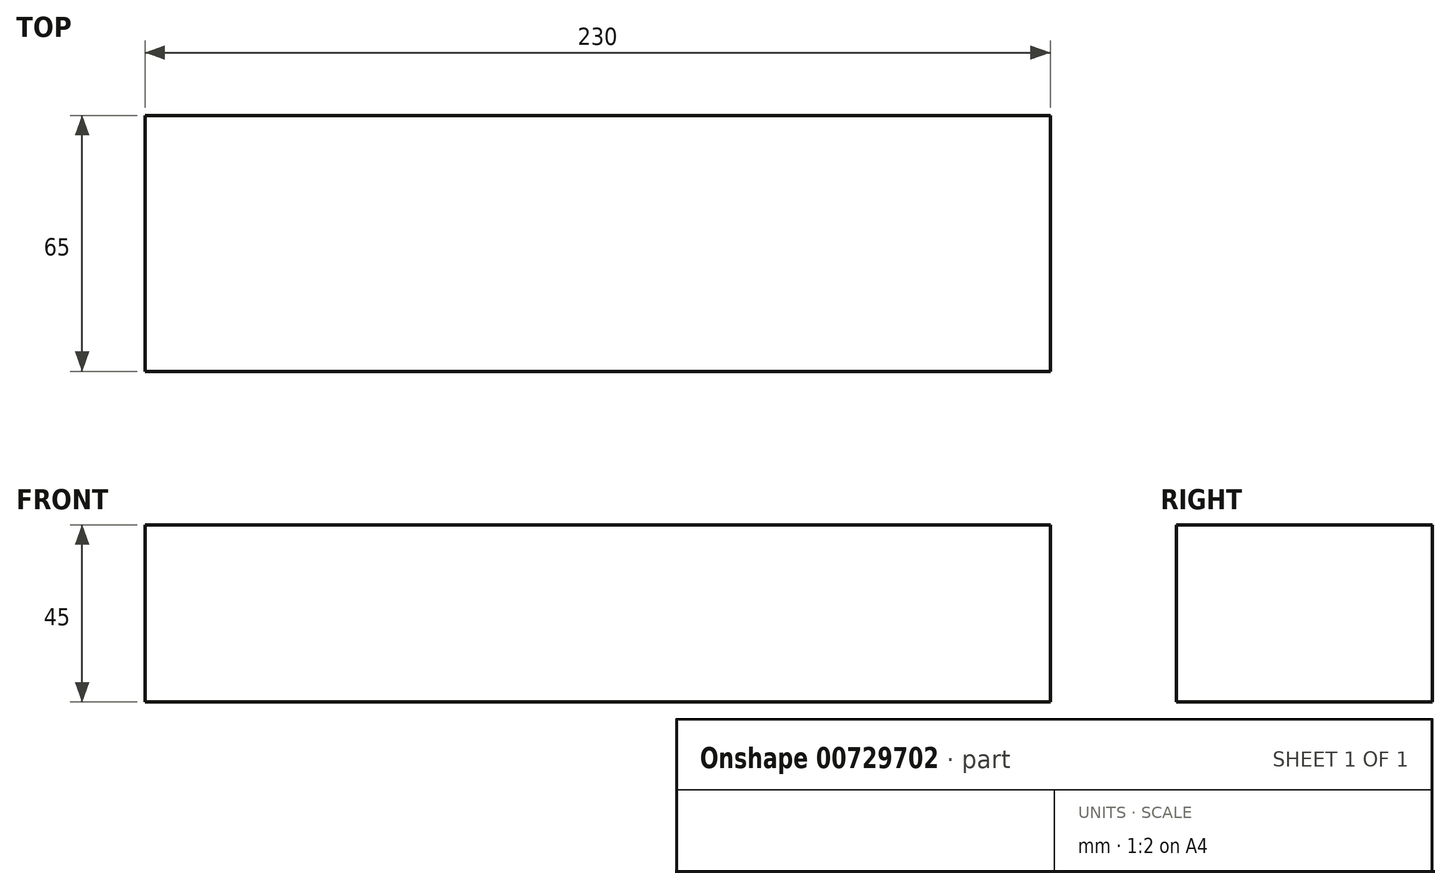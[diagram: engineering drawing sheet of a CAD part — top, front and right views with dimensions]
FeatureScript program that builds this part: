
annotation { "Feature Type Name" : "Feature", "Feature Type Description" : "" }
export const myFeature = defineFeature(function(context is Context, id is Id, definition is map)
    precondition{}
    {
        {
            var Q0;
            Q0=qCreatedBy(makeId("Top.planeOp"),FACE);
            var sketch = newSketch(context, id + "F0", { "sketchPlane" : qUnion([Q0])});
            skLineSegment(sketch, "E0.bottom", {"start": v(115, -32.5) * mm, "end": v(-115, -32.5) * mm});
            skLineSegment(sketch, "E0.top", {"start": v(115, 32.5) * mm, "end": v(-115, 32.5) * mm});
            skLineSegment(sketch, "E0.left", {"start": v(115, -32.5) * mm, "end": v(115, 32.5) * mm});
            skLineSegment(sketch, "E0.right", {"start": v(-115, -32.5) * mm, "end": v(-115, 32.5) * mm});
            skPoint(sketch, "E0.middle", {"position": v(0, 0) * mm});
            skSolve(sketch);
        }
        {
            var Q0;
            Q0=qSketchRegion(id+"F0",true);
            extrude(context, id + "F1", {"entities" : qUnion([Q0]), "depth" : 45 * mm, "offsetDistance" : 25 * mm});
        }
    });
